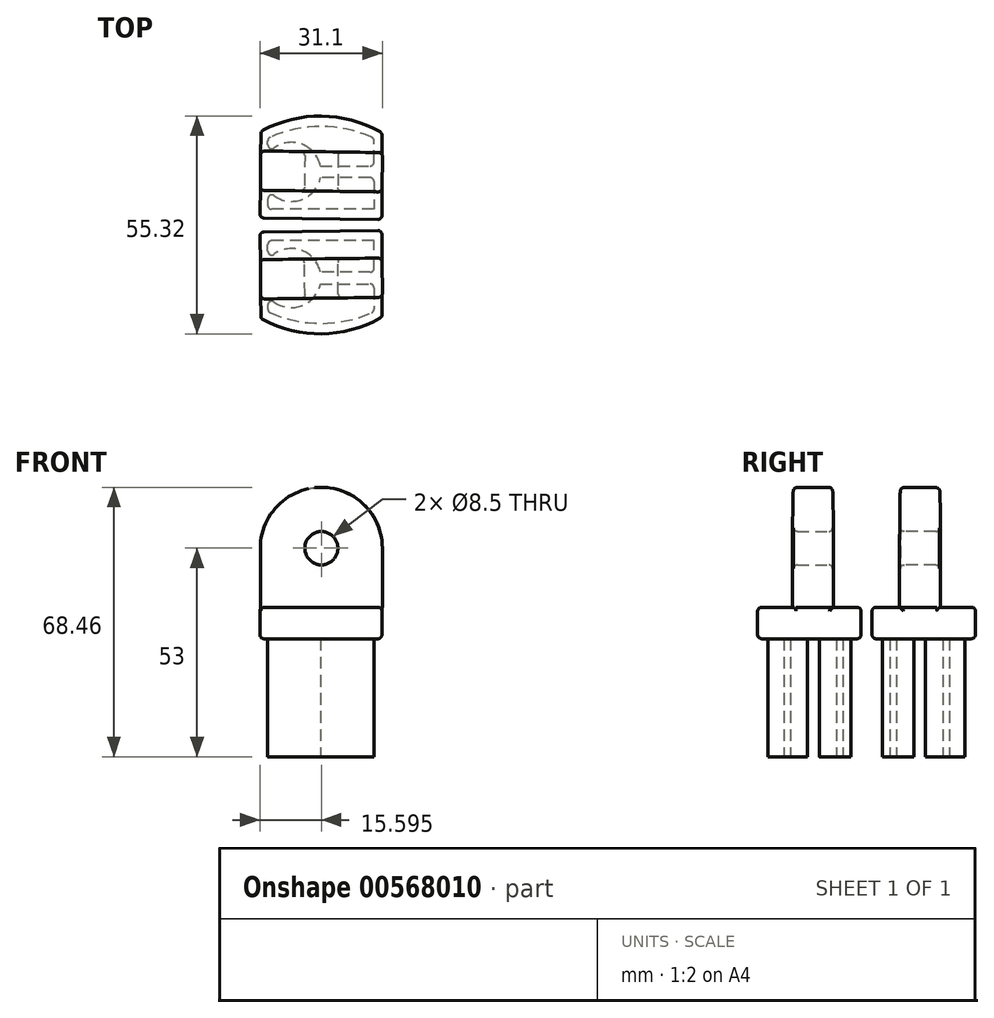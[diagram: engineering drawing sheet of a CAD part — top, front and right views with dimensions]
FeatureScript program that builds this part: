
annotation { "Feature Type Name" : "Feature", "Feature Type Description" : "" }
export const myFeature = defineFeature(function(context is Context, id is Id, definition is map)
    precondition{}
    {
        {
            var Q0;
            Q0=qCreatedBy(makeId("Top.planeOp"),FACE);
            var sketch = newSketch(context, id + "F0", { "sketchPlane" : qUnion([Q0])});
            skLineSegment(sketch, "E0.bottom", {"start": v(0, 0) * mm, "end": v(-27, 0) * mm});
            skLineSegment(sketch, "E0.top", {"start": v(0, -8) * mm, "end": v(-27, -8) * mm});
            skLineSegment(sketch, "E0.left", {"start": v(0, 0) * mm, "end": v(0, -8) * mm});
            skLineSegment(sketch, "E0.right", {"start": v(-27, 0) * mm, "end": v(-27, -8) * mm});
            skLineSegment(sketch, "E1.left", {"start": v(-27, 0) * mm, "end": v(-27, 3) * mm});
            skLineSegment(sketch, "E2.bottom", {"start": v(-27, 3) * mm, "end": v(0, 3) * mm});
            skLineSegment(sketch, "E2.top", {"start": v(-27, 10) * mm, "end": v(0, 10) * mm});
            skLineSegment(sketch, "E2.left", {"start": v(-27, 3) * mm, "end": v(-27, 10) * mm});
            skLineSegment(sketch, "E2.right", {"start": v(0, 3) * mm, "end": v(0, 10) * mm});
            skPoint(sketch, "E3.oppositeSnap0", {"position": v(-13.5, 11.8) * mm});
            skLineSegment(sketch, "E3.bottom", {"start": v(-27, 10) * mm, "end": v(-13.5, 10) * mm});
            skArc(sketch, "E4", {"start": v(0, 10) * mm, "mid": v(-13.5, 13) * mm, "end": v(-27, 10) * mm});
            skLineSegment(sketch, "E5.bottom", {"start": v(0, -8) * mm, "end": v(-21, -8) * mm});
            skLineSegment(sketch, "E5.left", {"start": v(0, -8) * mm, "end": v(0, 7) * mm});
            skCircle(sketch, "E6", {"center": v(-21, 1.5) * mm, "radius": 7.5 * mm});
            skSolve(sketch);
        }
        {
            var Q0;
            Q0=makeQuery(id+"F0.imprint","IMPRINT",FACE,{"disambiguationData":[TD([[makeQuery(id+"F0.imprint","IMPRINT",EDGE,{"derivedFrom":sQuery(id+"F0.wireOp",EDGE,"E2.top")}),-1.0]])]});
            var Q1;
            Q1=makeQuery(id+"F0.imprint","IMPRINT",FACE,{"disambiguationData":[TD([[makeQuery(id+"F0.imprint","IMPRINT",EDGE,{"derivedFrom":sQuery(id+"F0.wireOp",EDGE,"E2.top")}),1.0]])]});
            var Q2;
            {var subQ2=sQuery(id+"F0.wireOp",EDGE,"E0.top");Q2=makeQuery(id+"F0.imprint","IMPRINT",FACE,{"disambiguationData":[TD([[makeQuery(id+"F0.imprint","IMPRINT",EDGE,{"derivedFrom":subQ2}),-1.0]])]});}
            extrude(context, id + "F1", {"entities" : qUnion([Q0, Q1, Q2]), "depth" : 30 * mm, "offsetDistance" : 25 * mm});
        }
        {
            var Q0;
            Q0=makeQuery(id+"F1.opExtrude","CAP_FACE",FACE,{"disambiguationData":[OSD([sQuery(id+"F0.wireOp",EDGE,"E0.bottom"),sQuery(id+"F0.wireOp",EDGE,"E0.top"),sQuery(id+"F0.wireOp",EDGE,"E0.right"),sQuery(id+"F0.wireOp",EDGE,"E5.bottom"),sQuery(id+"F0.wireOp",EDGE,"E5.left"),sQuery(id+"F0.wireOp",EDGE,"E6")])],"isStart":false});
            var sketch = newSketch(context, id + "F2", { "sketchPlane" : qUnion([Q0])});
            skLineSegment(sketch, "E7", {"start": v(0, -8) * mm, "end": v(2, -8) * mm});
            skLineSegment(sketch, "E8", {"start": v(-27, -8) * mm, "end": v(-29, -8) * mm});
            skLineSegment(sketch, "E9", {"start": v(-28.73, 11.8) * mm, "end": v(-29, -10.2) * mm});
            skLineSegment(sketch, "E10", {"start": v(-29, -10.2) * mm, "end": v(2, -10.6) * mm});
            skLineSegment(sketch, "E11", {"start": v(2, -10.6) * mm, "end": v(2, 11.4) * mm});
            skArc(sketch, "E12", {"start": v(2, 11.4) * mm, "mid": v(-13.31, 15.66) * mm, "end": v(-28.73, 11.8) * mm});
            skPoint(sketch, "E13", {"position": v(-28.91, -3.2) * mm});
            skPoint(sketch, "E14.end.orphan", {"position": v(0, 9.97) * mm});
            skSolve(sketch);
        }
        {
            var Q0;
            {var subQ0=sQuery(id+"F2.wireOp",EDGE,"E12");Q0=makeQuery(id+"F2.imprint","IMPRINT",FACE,{"disambiguationData":[TD([[makeQuery(id+"F2.imprint","IMPRINT",EDGE,{"derivedFrom":subQ0}),1.0]])]});}
            var Q1;
            {var subQ1=sQuery(id+"F0.wireOp",EDGE,"E0.bottom");Q1=makeQuery(id+"F2.imprint","IMPRINT",FACE,{"disambiguationData":[TD([[makeQuery(id+"F2.imprint","IMPRINT",EDGE,{"derivedFrom":makeQuery(id+"F1.opExtrude","CAP_EDGE",EDGE,{"disambiguationData":[OSD([subQ1])],"isStart":false})}),1.0]])]});}
            var Q2;
            {var subQ0=sQuery(id+"F2.wireOp",EDGE,"E10");Q2=makeQuery(id+"F2.imprint","IMPRINT",FACE,{"disambiguationData":[TD([[makeQuery(id+"F2.imprint","IMPRINT",EDGE,{"derivedFrom":subQ0}),1.0]])]});}
            extrude(context, id + "F3", {"entities" : qUnion([Q0, Q1, Q2]), "depth" : 8 * mm, "offsetDistance" : 25 * mm});
        }
        {
            var Q0;
            Q0=makeQuery(id+"F3.opExtrude","CAP_FACE",FACE,{"disambiguationData":[OSD([sQuery(id+"F2.wireOp",EDGE,"E9"),sQuery(id+"F2.wireOp",EDGE,"E10"),sQuery(id+"F2.wireOp",EDGE,"EPf6RmNQ-HySo-Cs77-po54-DUGT3Q2lf2zp"),sQuery(id+"F2.wireOp",EDGE,"jiiT1BHf-txtQ-utGD-3t5S-hAZlwz8qiANK")])],"isStart":false});
            var sketch = newSketch(context, id + "F4", { "sketchPlane" : qUnion([Q0])});
            skLineSegment(sketch, "E15", {"start": v(-29, -10.2) * mm, "end": v(-28.91, -3.2) * mm});
            skLineSegment(sketch, "E16", {"start": v(-28.91, -3.2) * mm, "end": v(2, -3.6) * mm});
            skSolve(sketch);
        }
        {
            var Q0;
            Q0=sQuery(id+"F4.wireOp",EDGE,"E16");
            extrude(context, id + "F5", {"bodyType" : ToolBodyType.SURFACE, "surfaceEntities" : qUnion([Q0]), "depth" : 15 * mm});
        }
        {
            var Q0;
            Q0=makeQuery(id+"F5.opExtrude","SWEPT_FACE",FACE,{"disambiguationData":[OSD([sQuery(id+"F4.wireOp",EDGE,"E16")])]});
            var sketch = newSketch(context, id + "F6", { "sketchPlane" : qUnion([Q0])});
            skCircle(sketch, "E17", {"center": v(-13.41, 53) * mm, "radius": 15.46 * mm});
            skCircle(sketch, "E18", {"center": v(-13.41, 53) * mm, "radius": 4.25 * mm});
            skSolve(sketch);
        }
        {
            var Q0;
            {var subQ2=makeQuery(id+"F5.opExtrude","SWEPT_EDGE",EDGE,{"disambiguationData":[OSD([sQuery(id+"F4.wireOp",VERTEX,"E16.start")])]});Q0=makeQuery(id+"F6.imprint","IMPRINT",FACE,{"disambiguationData":[TD([[makeQuery(id+"F6.imprint","IMPRINT",EDGE,{"derivedFrom":subQ2}),-1.0]])]});}
            var Q1;
            {var subQ1=sQuery(id+"F4.wireOp",EDGE,"E16");var subQ5=sQuery(id+"F6.wireOp",EDGE,"E18");var subQ6=makeQuery(id+"F5.opExtrude","CAP_EDGE",EDGE,{"disambiguationData":[OSD([subQ1])],"isStart":false});var subQ7=makeQuery(id+"F6.imprint","INTERSECT",VERTEX,{"disambiguationData":[OD(0.0)],"derivedFrom":[subQ6,subQ5]});Q1=makeQuery(id+"F6.imprint","IMPRINT",FACE,{"disambiguationData":[TD([[makeQuery(id+"F6.imprint","IMPRINT",EDGE,{"disambiguationData":[TD([[subQ7,-1.0]])],"derivedFrom":subQ5}),-1.0]])]});}
            var Q2;
            {var subQ2=makeQuery(id+"F5.opExtrude","SWEPT_EDGE",EDGE,{"disambiguationData":[OSD([sQuery(id+"F4.wireOp",VERTEX,"E16.end")])]});Q2=makeQuery(id+"F6.imprint","IMPRINT",FACE,{"disambiguationData":[TD([[makeQuery(id+"F6.imprint","IMPRINT",EDGE,{"derivedFrom":subQ2}),1.0]])]});}
            var Q3;
            {var subQ1=makeQuery(id+"F5.opExtrude","CAP_EDGE",EDGE,{"disambiguationData":[OSD([sQuery(id+"F4.wireOp",EDGE,"E16")])],"isStart":false});var subQ4=sQuery(id+"F6.wireOp",EDGE,"E18");var subQ5=makeQuery(id+"F6.imprint","INTERSECT",VERTEX,{"disambiguationData":[OD(0.0)],"derivedFrom":[subQ1,subQ4]});Q3=makeQuery(id+"F6.imprint","IMPRINT",FACE,{"disambiguationData":[TD([[makeQuery(id+"F6.imprint","IMPRINT",EDGE,{"disambiguationData":[TD([[subQ5,1.0]])],"derivedFrom":subQ4}),-1.0]])]});}
            extrude(context, id + "F7", {"entities" : qUnion([Q0, Q1, Q2, Q3]), "operationType" : NewBodyOperationType.ADD, "oppositeDirection" : true, "depth" : 10 * mm});
        }
        {
            var Q0;
            {var subQ1=sQuery(id+"F2.wireOp",EDGE,"jiiT1BHf-txtQ-utGD-3t5S-hAZlwz8qiANK");var subQ2=sQuery(id+"F2.wireOp",EDGE,"E9");Q0=makeQuery(id+"F7.boolean.opBoolean","SPLIT",EDGE,{"disambiguationData":[TD([makeQuery(id+"F3.opExtrude","SWEPT_FACE",FACE,{"disambiguationData":[OSD([subQ1])]})])],"derivedFrom":makeQuery(id+"F3.opExtrude","CAP_EDGE",EDGE,{"disambiguationData":[OSD([subQ2])],"isStart":false})});}
            var Q1;
            Q1=makeQuery(id+"F3.opExtrude","CAP_EDGE",EDGE,{"disambiguationData":[OSD([sQuery(id+"F2.wireOp",EDGE,"E10")])],"isStart":false});
            var Q2;
            {var subQ0=sQuery(id+"F2.wireOp",EDGE,"E10");var subQ2=sQuery(id+"F2.wireOp",EDGE,"E9");Q2=makeQuery(id+"F7.boolean.opBoolean","SPLIT",EDGE,{"disambiguationData":[TD([makeQuery(id+"F3.opExtrude","SWEPT_FACE",FACE,{"disambiguationData":[OSD([subQ0])]})])],"derivedFrom":makeQuery(id+"F3.opExtrude","CAP_EDGE",EDGE,{"disambiguationData":[OSD([subQ2])],"isStart":false})});}
            var Q3;
            {var subQ0=sQuery(id+"F2.wireOp",EDGE,"EPf6RmNQ-HySo-Cs77-po54-DUGT3Q2lf2zp");var subQ1=makeQuery(id+"F3.opExtrude","SWEPT_FACE",FACE,{"disambiguationData":[OSD([subQ0])]});var subQ2=sQuery(id+"F2.wireOp",EDGE,"E10");var subQ5=makeQuery(id+"F3.opExtrude","CAP_FACE",FACE,{"disambiguationData":[OSD([sQuery(id+"F2.wireOp",EDGE,"E9"),subQ2,subQ0,sQuery(id+"F2.wireOp",EDGE,"jiiT1BHf-txtQ-utGD-3t5S-hAZlwz8qiANK")])],"isStart":false});Q3=makeQuery(id+"F7.boolean.opBoolean","SPLIT",EDGE,{"disambiguationData":[topologyDisambiguationEdgeConnected([subQ5,subQ1]),TD([makeQuery(id+"F3.opExtrude","SWEPT_FACE",FACE,{"disambiguationData":[OSD([subQ2])]})])],"derivedFrom":makeQuery(id+"F3.opExtrude","CAP_EDGE",EDGE,{"disambiguationData":[OSD([subQ0])],"isStart":false})});}
            fillet(context, id + "F8", {"entities" : qUnion([Q0, Q1, Q2, Q3]), "radius" : 1 * mm, "tangentPropagation" : true, "allowEdgeOverflow" : false});
        }
        {
            var Q0;
            Q0=makeQuery(id+"F7.opExtrude","CAP_EDGE",EDGE,{"disambiguationData":[OSD([sQuery(id+"F6.wireOp",EDGE,"E17")])],"isStart":true});
            var Q1;
            Q1=makeQuery(id+"F7.opExtrude","CAP_EDGE",EDGE,{"disambiguationData":[OSD([sQuery(id+"F6.wireOp",EDGE,"E17")])],"isStart":false});
            var Q2;
            Q2=makeQuery(id+"F7.opExtrude","CAP_EDGE",EDGE,{"disambiguationData":[OSD([sQuery(id+"F4.wireOp",VERTEX,"E16.start")])],"isStart":true});
            var Q3;
            Q3=makeQuery(id+"F7.opExtrude","CAP_EDGE",EDGE,{"disambiguationData":[OSD([sQuery(id+"F4.wireOp",VERTEX,"E16.end")])],"isStart":false});
            var Q4;
            Q4=makeQuery(id+"F7.opExtrude","CAP_EDGE",EDGE,{"disambiguationData":[OSD([sQuery(id+"F4.wireOp",VERTEX,"E16.start")])],"isStart":false});
            fillet(context, id + "F9", {"entities" : qUnion([Q0, Q1, Q2, Q3, Q4]), "radius" : 1 * mm, "tangentPropagation" : true, "allowEdgeOverflow" : false});
        }
        {
            var Q0;
            Q0=makeQuery(id+"F3.opExtrude","SWEPT_EDGE",EDGE,{"disambiguationData":[OSD([sQuery(id+"F2.wireOp",EDGE,"E9"),sQuery(id+"F2.wireOp",EDGE,"E10")])]});
            var Q1;
            Q1=makeQuery(id+"F3.opExtrude","SWEPT_EDGE",EDGE,{"disambiguationData":[OSD([sQuery(id+"F2.wireOp",EDGE,"E10"),sQuery(id+"F2.wireOp",EDGE,"EPf6RmNQ-HySo-Cs77-po54-DUGT3Q2lf2zp")])]});
            var Q2;
            Q2=makeQuery(id+"F3.opExtrude","SWEPT_EDGE",EDGE,{"disambiguationData":[OSD([sQuery(id+"F2.wireOp",EDGE,"EPf6RmNQ-HySo-Cs77-po54-DUGT3Q2lf2zp"),sQuery(id+"F2.wireOp",EDGE,"jiiT1BHf-txtQ-utGD-3t5S-hAZlwz8qiANK")])]});
            var Q3;
            {var subQ0=sQuery(id+"F4.wireOp",EDGE,"E16");var subQ1=sQuery(id+"F2.wireOp",EDGE,"EPf6RmNQ-HySo-Cs77-po54-DUGT3Q2lf2zp");var subQ2=makeQuery(id+"F3.opExtrude","SWEPT_FACE",FACE,{"disambiguationData":[OSD([subQ1])]});var subQ3=sQuery(id+"F2.wireOp",EDGE,"jiiT1BHf-txtQ-utGD-3t5S-hAZlwz8qiANK");var subQ4=makeQuery(id+"F3.opExtrude","CAP_FACE",FACE,{"disambiguationData":[OSD([sQuery(id+"F2.wireOp",EDGE,"E9"),sQuery(id+"F2.wireOp",EDGE,"E10"),subQ1,subQ3])],"isStart":false});var subQ5=makeQuery(id+"F7.opExtrude","SWEPT_FACE",FACE,{"disambiguationData":[OSD([subQ0])]});var subQ6=makeQuery(id+"F3.opExtrude","CAP_EDGE",EDGE,{"disambiguationData":[OSD([subQ1])],"isStart":false});Q3=makeQuery(id+"F9.opFillet","MERGE",EDGE,{"derivedFrom":[makeQuery(id+"F7.boolean.opBoolean","SPLIT",EDGE,{"disambiguationData":[topologyDisambiguationEdgeConnected([subQ2,subQ5])],"derivedFrom":subQ6}),makeQuery(id+"F7.boolean.opBoolean","SPLIT",EDGE,{"disambiguationData":[topologyDisambiguationEdgeConnected([subQ4,subQ2]),TD([makeQuery(id+"F3.opExtrude","SWEPT_FACE",FACE,{"disambiguationData":[OSD([subQ3])]})])],"derivedFrom":subQ6})]});}
            var Q4;
            Q4=makeQuery(id+"F1.opExtrude","SWEPT_EDGE",EDGE,{"disambiguationData":[OSD([sQuery(id+"F0.wireOp",EDGE,"E2.top"),sQuery(id+"F0.wireOp",EDGE,"E2.right"),sQuery(id+"F0.wireOp",EDGE,"E4")])]});
            var Q5;
            Q5=makeQuery(id+"F1.opExtrude","SWEPT_EDGE",EDGE,{"disambiguationData":[OSD([sQuery(id+"F0.wireOp",EDGE,"E2.bottom"),sQuery(id+"F0.wireOp",EDGE,"E5.left")])]});
            var Q6;
            Q6=makeQuery(id+"F1.opExtrude","SWEPT_EDGE",EDGE,{"disambiguationData":[OSD([sQuery(id+"F0.wireOp",EDGE,"E0.bottom"),sQuery(id+"F0.wireOp",EDGE,"E5.left")])]});
            var Q7;
            Q7=makeQuery(id+"F1.opExtrude","SWEPT_EDGE",EDGE,{"disambiguationData":[OSD([sQuery(id+"F0.wireOp",EDGE,"E5.bottom"),sQuery(id+"F0.wireOp",EDGE,"E5.left")])]});
            var Q8;
            Q8=makeQuery(id+"F1.opExtrude","SWEPT_EDGE",EDGE,{"disambiguationData":[OSD([sQuery(id+"F0.wireOp",EDGE,"E0.top"),sQuery(id+"F0.wireOp",EDGE,"E0.right")])]});
            var Q9;
            Q9=makeQuery(id+"F1.opExtrude","SWEPT_EDGE",EDGE,{"disambiguationData":[OSD([sQuery(id+"F0.wireOp",EDGE,"E0.right"),sQuery(id+"F0.wireOp",EDGE,"E6")])]});
            var Q10;
            Q10=makeQuery(id+"F1.opExtrude","SWEPT_EDGE",EDGE,{"disambiguationData":[OSD([sQuery(id+"F0.wireOp",EDGE,"E2.left"),sQuery(id+"F0.wireOp",EDGE,"E6")])]});
            fillet(context, id + "F10", {"entities" : qUnion([Q0, Q1, Q2, Q3, Q4, Q5, Q6, Q7, Q8, Q9, Q10]), "radius" : 1 * mm, "tangentPropagation" : true, "allowEdgeOverflow" : false});
        }
        {
            var Q0;
            Q0=makeQuery(id+"F1.opExtrude","SWEPT_EDGE",EDGE,{"disambiguationData":[OSD([sQuery(id+"F0.wireOp",EDGE,"E2.left"),sQuery(id+"F0.wireOp",EDGE,"E3.bottom"),sQuery(id+"F0.wireOp",EDGE,"E4")])]});
            fillet(context, id + "F11", {"entities" : qUnion([Q0]), "radius" : 1 * mm, "tangentPropagation" : true, "allowEdgeOverflow" : false});
        }
        {
            var Q0;
            Q0=makeQuery(id+"F5.opExtrude","SWEPT_BODY",BODY,{"disambiguationData":[OSD([sQuery(id+"F4.wireOp",EDGE,"E16")])]});
            deleteBodies(context, id + "F12", {"entities" : qUnion([Q0])});
        }
        {
            var Q0;
            Q0=makeQuery(id+"F7.opExtrude","CAP_EDGE",EDGE,{"disambiguationData":[OSD([sQuery(id+"F6.wireOp",EDGE,"E18")])],"isStart":false});
            var Q1;
            Q1=makeQuery(id+"F7.opExtrude","CAP_EDGE",EDGE,{"disambiguationData":[OSD([sQuery(id+"F6.wireOp",EDGE,"E18")])],"isStart":true});
            fillet(context, id + "F13", {"entities" : qUnion([Q0, Q1]), "radius" : 1 * mm, "tangentPropagation" : true, "allowEdgeOverflow" : false});
        }
        {
            var Q0;
            {var subQ0=sQuery(id+"F2.wireOp",EDGE,"E10");Q0=makeQuery(id+"F2.imprint","IMPRINT",FACE,{"disambiguationData":[TD([[makeQuery(id+"F2.imprint","IMPRINT",EDGE,{"derivedFrom":subQ0}),1.0]])]});}
            var Q1;
            {var subQ1=sQuery(id+"F0.wireOp",EDGE,"E0.bottom");Q1=makeQuery(id+"F2.imprint","IMPRINT",FACE,{"disambiguationData":[TD([[makeQuery(id+"F2.imprint","IMPRINT",EDGE,{"derivedFrom":makeQuery(id+"F1.opExtrude","CAP_EDGE",EDGE,{"disambiguationData":[OSD([subQ1])],"isStart":false})}),1.0]])]});}
            var Q2;
            {var subQ0=sQuery(id+"F2.wireOp",EDGE,"E12");Q2=makeQuery(id+"F2.imprint","IMPRINT",FACE,{"disambiguationData":[TD([[makeQuery(id+"F2.imprint","IMPRINT",EDGE,{"derivedFrom":subQ0}),1.0]])]});}
            extrude(context, id + "F14", {"entities" : qUnion([Q0, Q1, Q2]), "depth" : 8 * mm});
        }
        {
            var Q0;
            Q0=makeQuery(id+"F14.opExtrude","CAP_EDGE",EDGE,{"disambiguationData":[OSD([sQuery(id+"F2.wireOp",EDGE,"E10")])],"isStart":false});
            var Q1;
            Q1=makeQuery(id+"F14.opExtrude","CAP_EDGE",EDGE,{"disambiguationData":[OSD([sQuery(id+"F2.wireOp",EDGE,"E12")])],"isStart":false});
            var Q2;
            Q2=makeQuery(id+"F14.opExtrude","SWEPT_EDGE",EDGE,{"disambiguationData":[OSD([sQuery(id+"F2.wireOp",EDGE,"E9"),sQuery(id+"F2.wireOp",EDGE,"E10")])]});
            var Q3;
            Q3=makeQuery(id+"F14.opExtrude","SWEPT_EDGE",EDGE,{"disambiguationData":[OSD([sQuery(id+"F2.wireOp",EDGE,"E9"),sQuery(id+"F2.wireOp",EDGE,"E12")])]});
            var Q4;
            Q4=makeQuery(id+"F14.opExtrude","SWEPT_EDGE",EDGE,{"disambiguationData":[OSD([sQuery(id+"F2.wireOp",EDGE,"E11"),sQuery(id+"F2.wireOp",EDGE,"E12")])]});
            var Q5;
            Q5=makeQuery(id+"F14.opExtrude","SWEPT_EDGE",EDGE,{"disambiguationData":[OSD([sQuery(id+"F2.wireOp",EDGE,"E10"),sQuery(id+"F2.wireOp",EDGE,"E11")])]});
            fillet(context, id + "F15", {"entities" : qUnion([Q0, Q1, Q2, Q3, Q4, Q5]), "radius" : 1 * mm, "tangentPropagation" : true, "allowEdgeOverflow" : false});
        }
        {
            var Q0;
            Q0=makeQuery(id+"F14.opExtrude","SWEPT_EDGE",EDGE,{"disambiguationData":[OSD([sQuery(id+"F2.wireOp",EDGE,"E9"),sQuery(id+"F2.wireOp",EDGE,"E10")])]});
            var Q1;
            Q1=makeQuery(id+"F14.opExtrude","SWEPT_EDGE",EDGE,{"disambiguationData":[OSD([sQuery(id+"F2.wireOp",EDGE,"E9"),sQuery(id+"F2.wireOp",EDGE,"E12")])]});
            var Q2;
            Q2=makeQuery(id+"F15.opFillet","BLEND_EDGE",EDGE,{"blendedFrom":[makeQuery(id+"F14.opExtrude","CAP_EDGE",EDGE,{"disambiguationData":[OSD([sQuery(id+"F2.wireOp",EDGE,"E9")])],"isStart":false}),makeQuery(id+"F14.opExtrude","CAP_EDGE",EDGE,{"disambiguationData":[OSD([sQuery(id+"F2.wireOp",EDGE,"E12")])],"isStart":false})],"blendedInto":[]});
            var Q3;
            Q3=makeQuery(id+"F15.opFillet","BLEND_EDGE",EDGE,{"blendedFrom":[makeQuery(id+"F14.opExtrude","CAP_EDGE",EDGE,{"disambiguationData":[OSD([sQuery(id+"F2.wireOp",EDGE,"E9")])],"isStart":false}),makeQuery(id+"F14.opExtrude","CAP_EDGE",EDGE,{"disambiguationData":[OSD([sQuery(id+"F2.wireOp",EDGE,"E10")])],"isStart":false})],"blendedInto":[]});
            var Q4;
            Q4=makeQuery(id+"F15.opFillet","BLEND_EDGE",EDGE,{"blendedFrom":[makeQuery(id+"F14.opExtrude","CAP_EDGE",EDGE,{"disambiguationData":[OSD([sQuery(id+"F2.wireOp",EDGE,"E10")])],"isStart":false}),makeQuery(id+"F14.opExtrude","CAP_EDGE",EDGE,{"disambiguationData":[OSD([sQuery(id+"F2.wireOp",EDGE,"E11")])],"isStart":false})],"blendedInto":[]});
            var Q5;
            Q5=makeQuery(id+"F14.opExtrude","SWEPT_EDGE",EDGE,{"disambiguationData":[OSD([sQuery(id+"F2.wireOp",EDGE,"E10"),sQuery(id+"F2.wireOp",EDGE,"E11")])]});
            var Q6;
            Q6=makeQuery(id+"F14.opExtrude","SWEPT_EDGE",EDGE,{"disambiguationData":[OSD([sQuery(id+"F2.wireOp",EDGE,"E11"),sQuery(id+"F2.wireOp",EDGE,"E12")])]});
            var Q7;
            Q7=makeQuery(id+"F15.opFillet","BLEND_EDGE",EDGE,{"blendedFrom":[makeQuery(id+"F14.opExtrude","CAP_EDGE",EDGE,{"disambiguationData":[OSD([sQuery(id+"F2.wireOp",EDGE,"E11")])],"isStart":false}),makeQuery(id+"F14.opExtrude","CAP_EDGE",EDGE,{"disambiguationData":[OSD([sQuery(id+"F2.wireOp",EDGE,"E12")])],"isStart":false})],"blendedInto":[]});
            var Q8;
            Q8=makeQuery(id+"F14.opExtrude","CAP_EDGE",EDGE,{"disambiguationData":[OSD([sQuery(id+"F2.wireOp",EDGE,"E12")])],"isStart":true});
            var Q9;
            Q9=makeQuery(id+"F3.opExtrude","CAP_EDGE",EDGE,{"disambiguationData":[OSD([sQuery(id+"F2.wireOp",EDGE,"E12")])],"isStart":true});
            var Q10;
            Q10=makeQuery(id+"F3.opExtrude","CAP_EDGE",EDGE,{"disambiguationData":[OSD([sQuery(id+"F2.wireOp",EDGE,"E11")])],"isStart":true});
            fillet(context, id + "F16", {"entities" : qUnion([Q0, Q1, Q2, Q3, Q4, Q5, Q6, Q7, Q8, Q9, Q10]), "radius" : 1 * mm, "tangentPropagation" : true, "allowEdgeOverflow" : false});
        }
        {
            var Q0;
            Q0=makeQuery(id+"F3.opExtrude","CAP_EDGE",EDGE,{"disambiguationData":[OSD([sQuery(id+"F2.wireOp",EDGE,"E12")])],"isStart":false});
            var Q1;
            {var subQ0=sQuery(id+"F2.wireOp",EDGE,"E10");Q1=makeQuery(id+"F15.opFillet","BLEND_EDGE",EDGE,{"blendedFrom":[makeQuery(id+"F14.opExtrude","SWEPT_EDGE",EDGE,{"disambiguationData":[OSD([subQ0,sQuery(id+"F2.wireOp",EDGE,"E11")])]}),makeQuery(id+"F14.opExtrude","CAP_EDGE",EDGE,{"disambiguationData":[OSD([subQ0])],"isStart":false})],"blendedInto":[]});}
            var Q2;
            {var subQ0=sQuery(id+"F4.wireOp",EDGE,"E16");var subQ1=sQuery(id+"F2.wireOp",EDGE,"E11");var subQ2=makeQuery(id+"F3.opExtrude","SWEPT_FACE",FACE,{"disambiguationData":[OSD([subQ1])]});var subQ3=sQuery(id+"F2.wireOp",EDGE,"E12");var subQ4=makeQuery(id+"F3.opExtrude","CAP_FACE",FACE,{"disambiguationData":[OSD([sQuery(id+"F2.wireOp",EDGE,"E9"),sQuery(id+"F2.wireOp",EDGE,"E10"),subQ1,subQ3])],"isStart":false});var subQ5=makeQuery(id+"F7.opExtrude","SWEPT_FACE",FACE,{"disambiguationData":[OSD([subQ0])]});var subQ6=makeQuery(id+"F3.opExtrude","CAP_EDGE",EDGE,{"disambiguationData":[OSD([subQ1])],"isStart":false});Q2=makeQuery(id+"F9.opFillet","MERGE",EDGE,{"derivedFrom":[makeQuery(id+"F7.boolean.opBoolean","SPLIT",EDGE,{"disambiguationData":[topologyDisambiguationEdgeConnected([subQ2,subQ5])],"derivedFrom":subQ6}),makeQuery(id+"F7.boolean.opBoolean","SPLIT",EDGE,{"disambiguationData":[topologyDisambiguationEdgeConnected([subQ4,subQ2]),TD([makeQuery(id+"F3.opExtrude","SWEPT_FACE",FACE,{"disambiguationData":[OSD([subQ3])]})])],"derivedFrom":subQ6})]});}
            var Q3;
            {var subQ0=sQuery(id+"F2.wireOp",EDGE,"E12");Q3=makeQuery(id+"F15.opFillet","BLEND_EDGE",EDGE,{"blendedFrom":[makeQuery(id+"F14.opExtrude","SWEPT_EDGE",EDGE,{"disambiguationData":[OSD([sQuery(id+"F2.wireOp",EDGE,"E9"),subQ0])]}),makeQuery(id+"F14.opExtrude","CAP_EDGE",EDGE,{"disambiguationData":[OSD([subQ0])],"isStart":false})],"blendedInto":[]});}
            var Q4;
            {var subQ1=sQuery(id+"F2.wireOp",EDGE,"E12");var subQ2=sQuery(id+"F2.wireOp",EDGE,"E9");Q4=makeQuery(id+"F7.boolean.opBoolean","SPLIT",EDGE,{"disambiguationData":[TD([makeQuery(id+"F3.opExtrude","SWEPT_FACE",FACE,{"disambiguationData":[OSD([subQ1])]})])],"derivedFrom":makeQuery(id+"F3.opExtrude","CAP_EDGE",EDGE,{"disambiguationData":[OSD([subQ2])],"isStart":false})});}
            fillet(context, id + "F17", {"entities" : qUnion([Q0, Q1, Q2, Q3, Q4]), "radius" : 1 * mm, "tangentPropagation" : true, "allowEdgeOverflow" : false});
        }
        {
            var Q0;
            Q0=qCreatedBy(makeId("Front.planeOp"),FACE);
            cPlane(context, id + "F18", {"entities" : qUnion([Q0]), "cplaneType" : CPlaneType.OFFSET, "offset" : 12 * mm, "width" : 150 * mm, "height" : 150 * mm});
        }
        {
            var Q0;
            Q0=makeQuery(id+"F1.opExtrude","SWEPT_BODY",BODY,{"disambiguationData":[OSD([sQuery(id+"F0.wireOp",EDGE,"E0.bottom"),sQuery(id+"F0.wireOp",EDGE,"E0.top"),sQuery(id+"F0.wireOp",EDGE,"E0.right"),sQuery(id+"F0.wireOp",EDGE,"E5.bottom"),sQuery(id+"F0.wireOp",EDGE,"E5.left"),sQuery(id+"F0.wireOp",EDGE,"E6")])]});
            var Q1;
            Q1=makeQuery(id+"F1.opExtrude","SWEPT_BODY",BODY,{"disambiguationData":[OSD([sQuery(id+"F0.wireOp",EDGE,"E2.bottom"),sQuery(id+"F0.wireOp",EDGE,"E2.left"),sQuery(id+"F0.wireOp",EDGE,"E2.right"),sQuery(id+"F0.wireOp",EDGE,"E4"),sQuery(id+"F0.wireOp",EDGE,"E5.left"),sQuery(id+"F0.wireOp",EDGE,"E6")])]});
            var Q2;
            Q2=makeQuery(id+"F3.opExtrude","SWEPT_BODY",BODY,{"disambiguationData":[OSD([sQuery(id+"F0.wireOp",EDGE,"E0.bottom"),sQuery(id+"F0.wireOp",EDGE,"E0.right"),sQuery(id+"F0.wireOp",EDGE,"E5.left"),sQuery(id+"F0.wireOp",EDGE,"E6"),sQuery(id+"F2.wireOp",EDGE,"E7"),sQuery(id+"F2.wireOp",EDGE,"E8"),sQuery(id+"F2.wireOp",EDGE,"E9"),sQuery(id+"F2.wireOp",EDGE,"E10"),sQuery(id+"F2.wireOp",EDGE,"E11")])]});
            var Q3;
            Q3=makeQuery(id+"F14.opExtrude","SWEPT_BODY",BODY,{"disambiguationData":[OSD([sQuery(id+"F2.wireOp",EDGE,"E9"),sQuery(id+"F2.wireOp",EDGE,"E10"),sQuery(id+"F2.wireOp",EDGE,"E11"),sQuery(id+"F2.wireOp",EDGE,"E12")])]});
            var Q4;
            Q4=qCreatedBy(id+"F18.planeOp",FACE);
            mirror(context, id + "F19", {"entities" : qUnion([Q0, Q1, Q2, Q3]), "mirrorPlane" : qUnion([Q4])});
        }
        {
            var Q0;
            Q0=makeQuery(id+"F19.opPattern","COPY",EDGE,{"derivedFrom":makeQuery(id+"F3.opExtrude","SWEPT_EDGE",EDGE,{"disambiguationData":[OSD([sQuery(id+"F2.wireOp",EDGE,"E9"),sQuery(id+"F2.wireOp",EDGE,"E12")])]}),"instanceName":"1"});
            var Q1;
            Q1=makeQuery(id+"F19.opPattern","COPY",EDGE,{"derivedFrom":makeQuery(id+"F3.opExtrude","SWEPT_EDGE",EDGE,{"disambiguationData":[OSD([sQuery(id+"F2.wireOp",EDGE,"E11"),sQuery(id+"F2.wireOp",EDGE,"E12")])]}),"instanceName":"1"});
            fillet(context, id + "F20", {"entities" : qUnion([Q0, Q1]), "radius" : 1 * mm, "tangentPropagation" : true, "allowEdgeOverflow" : false});
        }
        {
            var Q0;
            Q0=makeQuery(id+"F3.opExtrude","SWEPT_EDGE",EDGE,{"disambiguationData":[OSD([sQuery(id+"F2.wireOp",EDGE,"E9"),sQuery(id+"F2.wireOp",EDGE,"E12")])]});
            var Q1;
            Q1=makeQuery(id+"F3.opExtrude","SWEPT_EDGE",EDGE,{"disambiguationData":[OSD([sQuery(id+"F2.wireOp",EDGE,"E11"),sQuery(id+"F2.wireOp",EDGE,"E12")])]});
            fillet(context, id + "F21", {"entities" : qUnion([Q0, Q1]), "radius" : 1 * mm, "tangentPropagation" : true, "allowEdgeOverflow" : false});
        }
    });
